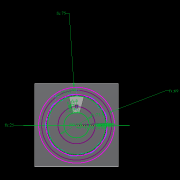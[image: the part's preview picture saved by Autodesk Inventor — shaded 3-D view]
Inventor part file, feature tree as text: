
AUTODESK INVENTOR PART (.ipt)
format: ipt  version: 2022.2 (Build 262287010, 287A)  size: 628,736 bytes
history: native  units: mm
features: extrude x27, other x19, sketch x17, pattern_circular x10, plane x5, fillet x2, move_body x2, revolve x2, draft x2, chamfer x2
ambient origin geometry x8: Origin, YZ Plane, XZ Plane, XY Plane, X Axis, Y Axis, Z Axis, Center Point
bodies: Solid5 (feature_tree)
feature tree (88):
  other  "CrossSection1"
  sketch  "Sketch7"  dims[d167=8.972256mm]
  other  "Roller1"
  other  "Roller2"
  sketch  "Sketch22"  dims[d173=10.814812mm]
  sketch  "Sketch2"  dims[d57=4.025mm d90=61.984365mm]
  sketch  "Sketch23"  dims[d201=75.0mm d232=0.0mm d233=3600.0mm]
  other  "RevRoller1"
  fillet  "Fillet1"  Radius=59.246882mm
  extrude  "Extrusion39"  Depth=61.984365mm
  pattern_circular  "Circular Pattern13"  Count=360  [1 undecoded]
  move_body  "Move Body7"
  revolve  "Revolution13"  [1 undecoded]
  fillet  "Fillet3"  Radius=0.025mm
  pattern_circular  "Circular Pattern14"  Count=24  [1 undecoded]
  move_body  "Move Body6"
  revolve  "Revolution14"  Angle=360.0deg
  other  "OuterRim_Top2"
  other  "OuterRim_Bottom2"
  plane  "Work Plane8"
  sketch  "Sketch49"  dims[d352=0.025mm]
  sketch  "Sketch50"  dims[d354=0.025mm]
  sketch  "Sketch51"  dims[d355=16.1595mm]
  extrude  "Extrusion40"  Depth=8.194mm
  extrude  "Extrusion41"  Depth=8.194mm
  extrude  "Extrusion42"  Depth=8.194mm
  extrude  "Extrusion43"  Depth=8.194mm
  sketch  "Sketch52"  dims[d356=16.159664mm]
  extrude  "Extrusion44"  Depth=8.194mm
  extrude  "Extrusion45"  TaperAngle=90.0deg  [1 undecoded]
  extrude  "Extrusion46"  Depth=8.194mm
  extrude  "Extrusion47"  Depth=8.194mm
  pattern_circular  "Circular Pattern32"  Angle=360.0deg  [1 undecoded]
  pattern_circular  "Circular Pattern33"  Angle=90.0deg  [1 undecoded]
  sketch  "Sketch57"  dims[d358=360.0deg]
  extrude  "Extrusion50"  Depth=0.1mm
  extrude  "Extrusion51"  Depth=8.194mm
  pattern_circular  "Circular Pattern34"  [2 undecoded]
  plane  "Work Plane9"
  extrude  "Extrusion52"  Depth=8.194mm
  plane  "Work Plane7"
  sketch  "Sketch47"  dims[d350=47.575427mm]
  extrude  "Rotor_Ring"  Depth=8.194mm
  draft  "FaceDraft2"
  sketch  "Sketch30"  dims[d343=16.1595mm d344=16.159664mm d345=0.025mm]
  plane  "Work Plane5"
  other  "Rotor Featurs"
  other  "RotorRim_Bottom"
  extrude  "Extrusion24"  Depth=11.193516mm
  extrude  "Extrusion25"  TaperAngle=0.0deg  [1 undecoded]
  extrude  "Extrusion26"  TaperAngle=0.0deg  [1 undecoded]
  pattern_circular  "Circular Pattern23"  [2 undecoded]
  sketch  "Sketch41"  dims[d347=0.1mm]
  extrude  "Extrusion27"  Depth=8.194mm
  extrude  "Extrusion28"  Depth=8.194mm
  pattern_circular  "Circular Pattern24"  [2 undecoded]
  extrude  "Extrusion29"  Depth=8.194mm
  extrude  "Extrusion30"  Depth=8.194mm
  extrude  "Extrusion31"  TaperAngle=90.0deg  [1 undecoded]
  pattern_circular  "Circular Pattern25"  Angle=90.0deg  [1 undecoded]
  sketch  "Sketch42"  dims[d348=0.1mm]
  extrude  "Extrusion32"  TaperAngle=90.0deg  [1 undecoded]
  extrude  "Extrusion33"  Depth=8.194mm
  extrude  "Extrusion34"  Depth=11.193516mm
  extrude  "Extrusion35"  TaperAngle=0.0deg  [1 undecoded]
  pattern_circular  "Circular Pattern26"  [2 undecoded]
  pattern_circular  "Circular Pattern27"  Count=2  [1 undecoded]
  chamfer  "Chamfer1"  Distance=2.5mm
  chamfer  "Chamfer2"  Distance=8.0mm
  draft  "FaceDraft4"
  plane  "Work Plane6"
  sketch  "Sketch43"  dims[d349=47.575591mm]
  extrude  "Extrusion37"  Depth=8.194mm
  extrude  "Extrusion38"  Depth=8.194mm TaperAngle=30.0deg
  other  "2D Equation Curve1"
  sketch  "Sketch40"  dims[d346=0.025mm]
  other  "Work Axis6"
  other  "Work Axis7"
  other  "Work Axis8"
  other  "Work Axis9"
  other  "Work Axis10"
  other  "Work Point1"
  other  "Work Point2"
  other  "Work Point3"
  other  "Work Point4"
  other  "Work Point5"
  sketch  "Sketch48"  dims[d351=0.025mm]
  sketch  "Sketch58"  dims[d359=0.5mm d360=240.0mm d361=360.0deg d363=1.308997mm d367=8.1mm d370=0.025mm d371=1.0mm d372=1.308997mm d373=90.0deg d374=0.5mm d375=240.0mm d376=360.0deg d378=90.0deg d379=0.1mm d380=0.025mm d381=0.025mm d382=0.025mm d383=0.025mm d384=11.193516mm d385=0.0mm d386=0.0mm d391=25.0mm d392=75.0mm d393=1.5mm d394=1.5mm d395=1.5mm d396=1.5mm d397=90.0deg d398=90.0deg d399=90.0deg d400=75.0mm d401=11.193516mm d402=0.0mm d486=0.436332mm d487=0.5mm d488=2.0mm d489=0.0mm d490=20.0mm d495=2.5mm d496=8.0mm d506=13.856406mm d507=55.5mm d508=8.0mm d509=0.05mm d510=2.5mm d511=30.0deg d512=12.0mm d513=6.0mm d514=0.2mm d515=30.0deg d516=131.0mm d517=65.5mm d518=0.2mm d519=100.0mm d520=120.0mm d521=2.0mm d522=150.0mm d530=50.0mm d531=5.5mm d532=5.5mm d533=5.5mm d534=85.75mm d535=73.5mm d536=61.25mm d537=24.5mm d538=3.0mm d539=2.4mm d540=0.0mm d541=0.0mm d542=0.0mm d543=5.5mm d544=3.0mm d545=0.0mm d546=90.0mm d547=360.0deg d549=3.0mm d550=3.0mm d551=2.4mm d552=0.0mm d553=5.596758mm d554=0.0mm d555=2.4mm d556=0.0mm d557=5.596758mm d558=0.0mm d559=5.596758mm d560=0.0mm d561=90.0mm d562=360.0deg d564=60.0mm d565=360.0deg d567=5.5mm d568=5.5mm d569=3.0mm d570=0.0mm d571=5.596758mm d572=0.0mm d573=3.0mm d574=0.0mm d575=5.596758mm d576=0.0mm d577=90.0mm d578=360.0deg d580=60.0mm d581=360.0deg d584=20.0mm d585=8.0mm d587=1.75mm d589=3.0mm d592=2.0mm d593=12.0mm d594=12.0mm d600=0.5mm d601=2.0mm d602=45.0deg d603=0.5mm d604=2.0mm d605=45.0deg d606=0.436332mm d607=0.5mm d608=0.0mm d609=20.0mm d611=360.0deg d613=0.0mm d614=0.0mm d617=0.99971mm d618=100.0mm d620=69.0mm d621=5.0mm d622=0.5mm d623=0.5mm d624=5.0mm d625=0.2mm d626=0.0mm d627=20.0mm d629=69.0mm d630=73.5mm d631=20.0mm d633=6.283185mm d635=5.5mm d636=3.0mm d637=7.0mm d638=4.0mm d639=5.596758mm d640=0.0mm d641=3.0mm d642=0.0mm d643=5.596758mm d644=0.0mm d645=4.0mm d646=0.0mm d647=20.0mm d649=6.283185mm d651=3.0mm d652=4.0mm d653=20.0mm d655=6.283185mm d657=7.0mm d658=5.5mm d659=5.596758mm d660=0.0mm d661=2.593516mm d662=0.0mm d663=5.596758mm d664=0.0mm d665=3.193516mm d666=0.0mm d679=50.0mm d680=360.0deg d682=50.0mm d683=360.0deg d694=6.35mm d695=6.35mm d696=6.4mm d697=5.45mm d698=11.194mm d699=0.0mm d700=8.194mm d701=0.0mm d702=60.0mm d703=360.0deg d705=-25.0mm d706=15.0deg d707=15.0deg d708=0.0mm d709=0.0mm d16=0.872665mm d17=0.872665mm d49=0.872665mm d50=0.872665mm d51=0.872665mm d52=0.872665mm d236=0.5mm d237=0.872665mm d238=0.5mm d239=0.872665mm d282=1.0mm d283=1.0mm d284=1.0mm d285=0.15mm d286=0.25mm d287=0.375mm d288=14.3117mm d289=0.75mm d290=20.594885mm d291=0.0625mm d292=0.75mm d293=0.375mm d405=0.5mm d406=0.872665mm d407=0.5mm d408=0.872665mm d413=0.5mm d414=0.872665mm d415=0.5mm d416=0.872665mm d417=0.5mm d418=0.872665mm d419=0.5mm d420=0.872665mm d421=0.872665mm d431=0.5mm d432=0.872665mm d433=0.5mm d434=0.872665mm d471=0.5mm d472=0.872665mm d473=0.5mm d474=0.872665mm d497=0.5mm d498=0.872665mm d499=0.5mm d500=0.872665mm d590=0.5mm d591=0.872665mm]
note: 21 required parameter values undecoded (feature->parameter linkage not recoverable at this tier; creation-order binding heuristic only, values carry confidence <= 0.55)